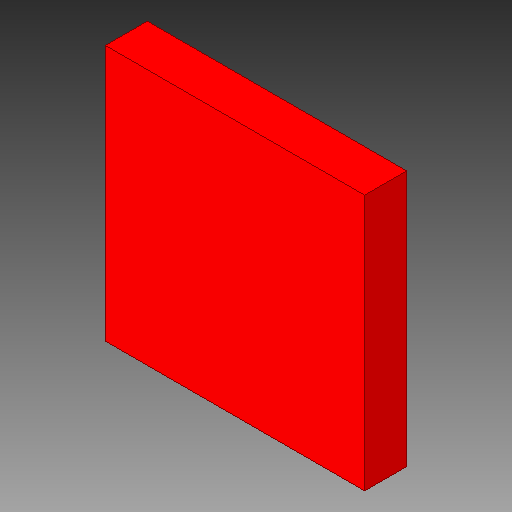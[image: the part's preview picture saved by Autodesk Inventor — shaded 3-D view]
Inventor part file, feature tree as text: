
AUTODESK INVENTOR PART (.ipt)
format: ipt  version: 2018 (Build 220112000, 112)  size: 80,896 bytes
history: native  units: in
note: dims shown in document units (in); Inventor stores cm internally (conversion verified against a paired STEP export)
features: other x1, extrude x1
ambient origin geometry x8: Origin, YZ Plane, XZ Plane, XY Plane, X Axis, Y Axis, Z Axis, Center Point
bodies: Solid1 (feature_tree)
feature tree (2):
  other  "PBTH, RST_142"
  extrude  "Extrusion1"  Depth=0.0394in TaperAngle=0.0deg
